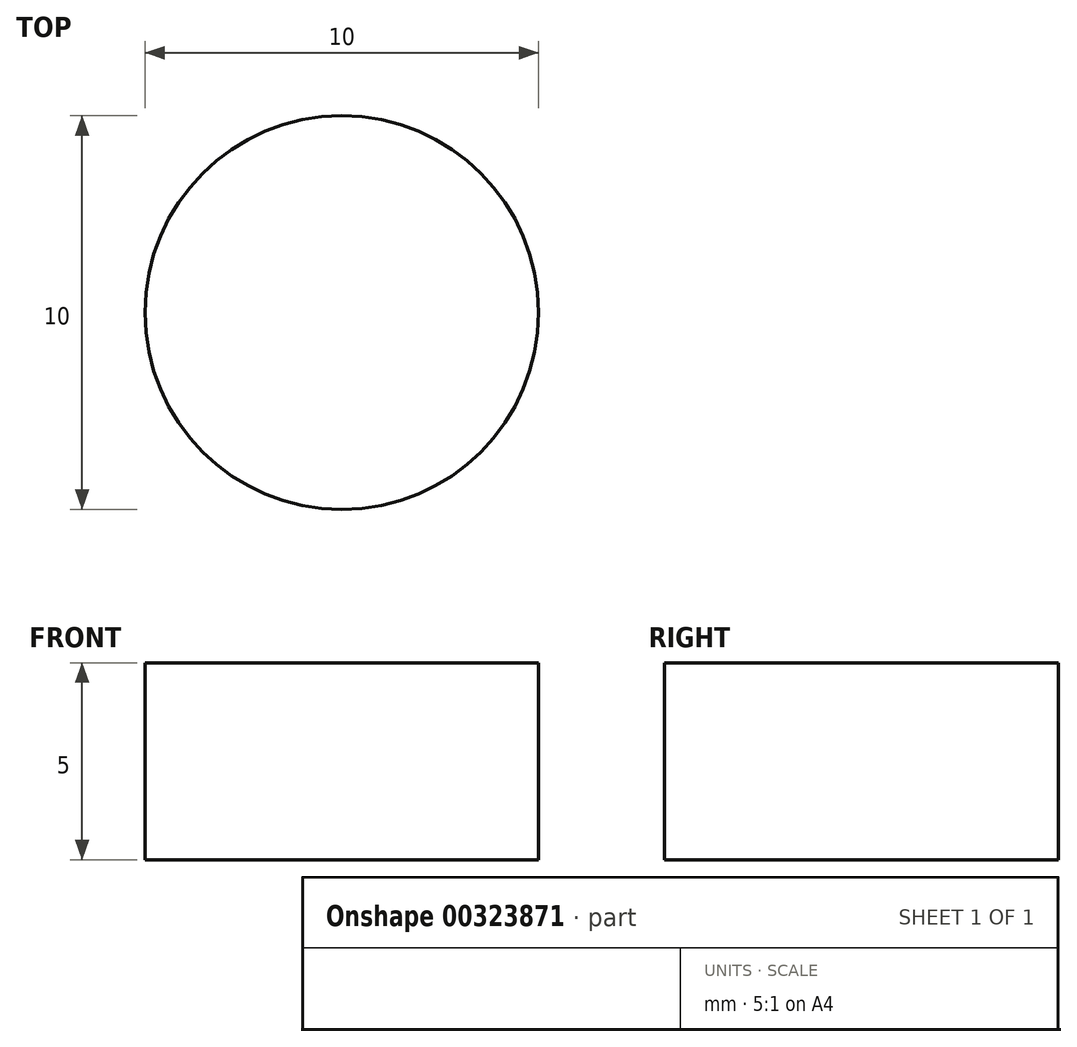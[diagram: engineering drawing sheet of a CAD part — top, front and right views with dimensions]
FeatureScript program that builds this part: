
annotation { "Feature Type Name" : "Feature", "Feature Type Description" : "" }
export const myFeature = defineFeature(function(context is Context, id is Id, definition is map)
    precondition{}
    {
        {
            var Q0;
            Q0=qCreatedBy(makeId("Top.planeOp"),FACE);
            var sketch = newSketch(context, id + "F0", { "sketchPlane" : qUnion([Q0])});
            skCircle(sketch, "E0", {"center": v(0, 0) * mm, "radius": 5 * mm});
            skSolve(sketch);
        }
        {
            var Q0;
            Q0=makeQuery(id+"F0.imprint","IMPRINT",FACE,{"disambiguationData":[TD([[makeQuery(id+"F0.imprint","IMPRINT",EDGE,{"derivedFrom":sQuery(id+"F0.wireOp",EDGE,"E0")}),1.0]])]});
            extrude(context, id + "F1", {"entities" : qUnion([Q0]), "depth" : 5 * mm});
        }
    });
